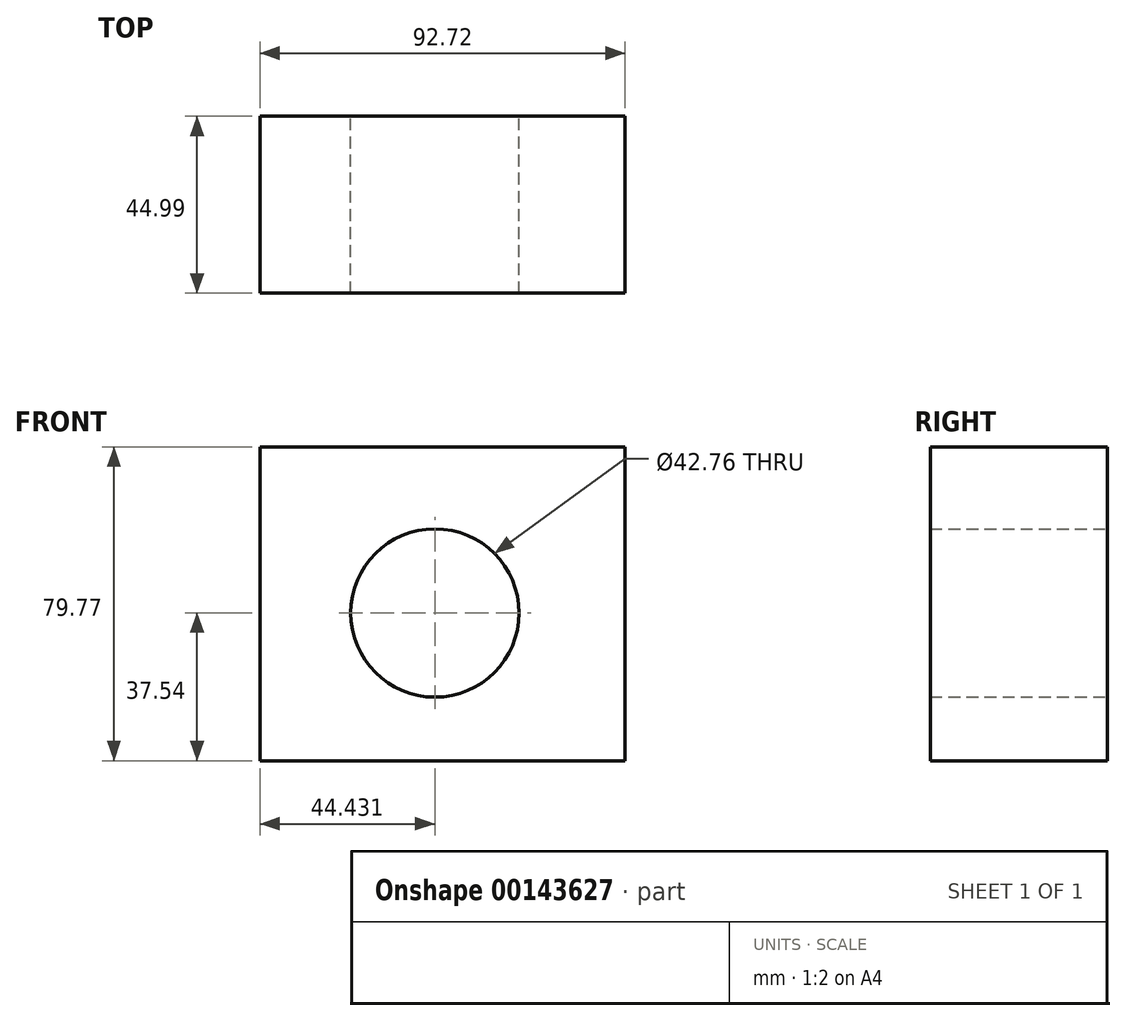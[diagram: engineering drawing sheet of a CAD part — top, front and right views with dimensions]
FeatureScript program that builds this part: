
annotation { "Feature Type Name" : "Feature", "Feature Type Description" : "" }
export const myFeature = defineFeature(function(context is Context, id is Id, definition is map)
    precondition{}
    {
        {
            var Q0;
            Q0=qCreatedBy(makeId("Front.planeOp"),FACE);
            var sketch = newSketch(context, id + "F0", { "sketchPlane" : qUnion([Q0])});
            skLineSegment(sketch, "E0.bottom", {"start": v(-48.83, 42.23) * mm, "end": v(43.9, 42.23) * mm});
            skLineSegment(sketch, "E0.top", {"start": v(-48.83, -37.54) * mm, "end": v(43.9, -37.54) * mm});
            skLineSegment(sketch, "E0.left", {"start": v(43.9, 42.23) * mm, "end": v(43.9, -37.54) * mm});
            skLineSegment(sketch, "E0.right", {"start": v(-48.83, 42.23) * mm, "end": v(-48.83, -37.54) * mm});
            skCircle(sketch, "E1", {"center": v(-4.4, 0) * mm, "radius": 21.38 * mm});
            skSolve(sketch);
        }
        {
            var Q0;
            Q0=makeQuery(id+"F0.imprint","IMPRINT",FACE,{"disambiguationData":[TD([[makeQuery(id+"F0.imprint","IMPRINT",EDGE,{"derivedFrom":sQuery(id+"F0.wireOp",EDGE,"E0.bottom")}),-1.0]])]});
            extrude(context, id + "F1", {"entities" : qUnion([Q0]), "depth" : 45 * mm});
        }
    });
